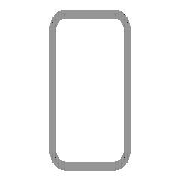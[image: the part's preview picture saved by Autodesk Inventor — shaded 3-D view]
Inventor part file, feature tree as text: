
AUTODESK INVENTOR PART (.ipt)
format: ipt  version: 2025 (Build 290162010, 162A)  size: 133,120 bytes
history: native  units: mm (DEFAULTED — no unit token found)
features: other x4, sketch x1, plane x1
ambient origin geometry x8: Origin, YZ Plane, XZ Plane, XY Plane, X Axis, Y Axis, Z Axis, Center Point
bodies: Solid1 (feature_tree), Body (feature_tree)
feature tree (6):
  parser-record x1  (decoder bookkeeping rows leaked as tree rows — omitted from the tree; the rows remain in map.json)
  other  "Driven Length"
  other  "Start Plane"
  other  "End Plane"
  sketch  "Sketch3"  dims[d3=2200.0mm d4=0.0mm d7=4.0mm d9=40.0mm d11=60.0mm d12=2.0mm d13=-0.0mm d14=2200.0mm d15=20.0mm d16=30.0mm d17=90.0deg d18=2200.0mm]
  plane  "Work Plane3"
